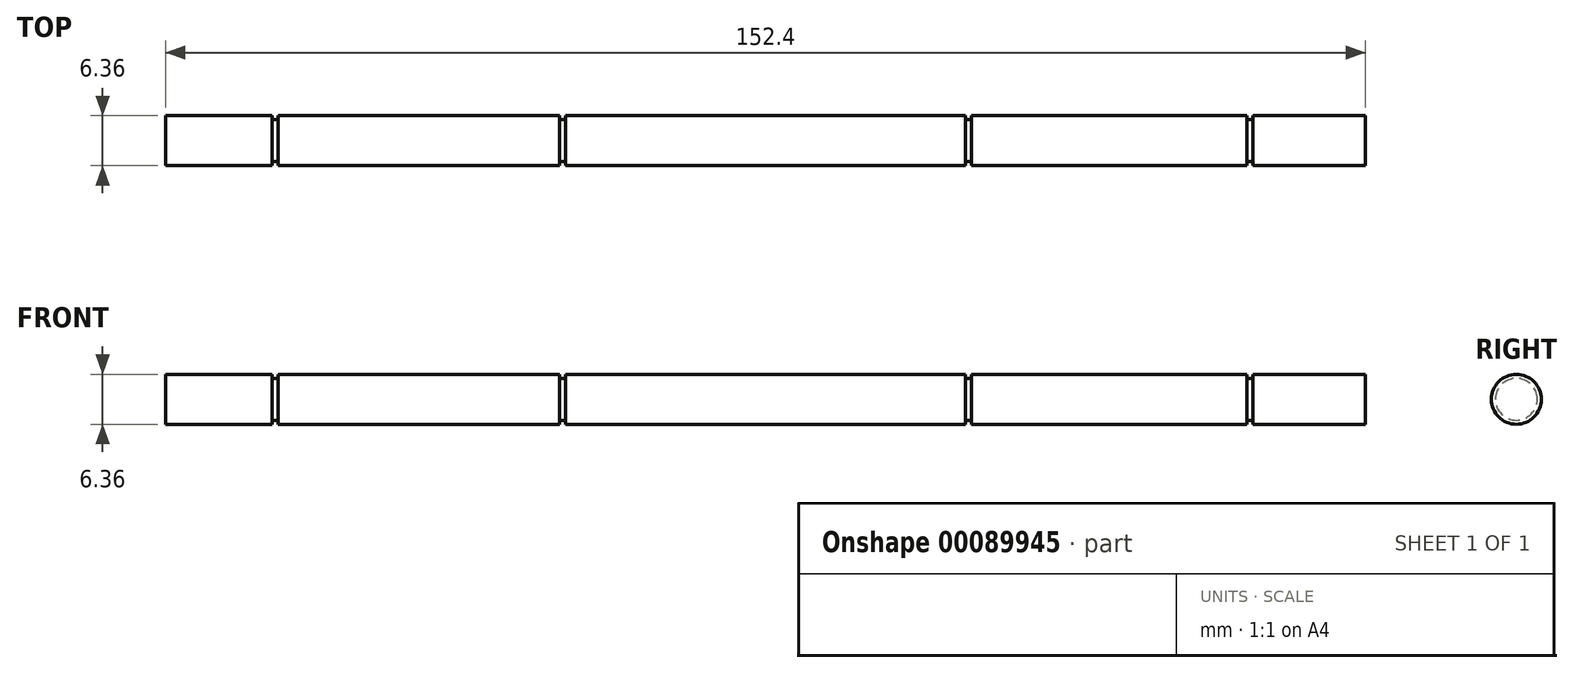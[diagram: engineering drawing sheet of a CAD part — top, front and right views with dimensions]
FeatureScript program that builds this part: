
annotation { "Feature Type Name" : "Feature", "Feature Type Description" : "" }
export const myFeature = defineFeature(function(context is Context, id is Id, definition is map)
    precondition{}
    {
        {
            var Q0;
            Q0=qCreatedBy(makeId("Right.planeOp"),FACE);
            var sketch = newSketch(context, id + "F0", { "sketchPlane" : qUnion([Q0])});
            skCircle(sketch, "E0", {"center": v(0, 0) * mm, "radius": 3.18 * mm});
            skSolve(sketch);
        }
        {
            var Q0;
            Q0 = qSketchRegion(id + "F0", true);
            extrude(context, id + "F1", {"entities" : qUnion([Q0]), "depth" : 152.4 * mm});
        }
        {
            var Q0;
            Q0=makeQuery(id+"F1.opExtrude","CAP_FACE",FACE,{"disambiguationData":[OSD([sQuery(id+"F0.wireOp",EDGE,"E0")])],"isStart":false});
            cPlane(context, id + "F2", {"entities" : qUnion([Q0]), "cplaneType" : CPlaneType.OFFSET, "offset" : 14.29 * mm, "oppositeDirection" : true, "width" : 152.4 * mm, "height" : 152.4 * mm});
        }
        {
            var Q0;
            Q0=qCreatedBy(id+"F2.planeOp",FACE);
            var sketch = newSketch(context, id + "F3", { "sketchPlane" : qUnion([Q0])});
            skCircle(sketch, "E1", {"center": v(0, 0) * mm, "radius": 3.18 * mm});
            skCircle(sketch, "E2", {"center": v(0, 0) * mm, "radius": 2.67 * mm});
            skSolve(sketch);
        }
        {
            var Q0;
            Q0 = qSketchRegion(id + "F3", true);
            extrude(context, id + "F4", {"entities" : qUnion([Q0]), "operationType" : NewBodyOperationType.REMOVE, "oppositeDirection" : true, "depth" : 0.74 * mm});
        }
        {
            var Q0;
            Q0=makeQuery(id+"F1.opExtrude","CAP_FACE",FACE,{"disambiguationData":[OSD([sQuery(id+"F0.wireOp",EDGE,"E0")])],"isStart":true});
            cPlane(context, id + "F5", {"entities" : qUnion([Q0]), "cplaneType" : CPlaneType.OFFSET, "offset" : 14.29 * mm, "oppositeDirection" : true, "width" : 152.4 * mm, "height" : 152.4 * mm});
        }
        {
            var Q0;
            Q0=qCreatedBy(id+"F5.planeOp",FACE);
            var sketch = newSketch(context, id + "F6", { "sketchPlane" : qUnion([Q0])});
            skCircle(sketch, "E3", {"center": v(0, 0) * mm, "radius": 3.18 * mm});
            skCircle(sketch, "E4", {"center": v(0, 0) * mm, "radius": 2.67 * mm});
            skSolve(sketch);
        }
        {
            var Q0;
            Q0 = qSketchRegion(id + "F6", true);
            extrude(context, id + "F7", {"entities" : qUnion([Q0]), "operationType" : NewBodyOperationType.REMOVE, "depth" : 0.74 * mm});
        }
        {
            var Q0;
            Q0=qCreatedBy(makeId("Right.planeOp"),FACE);
            cPlane(context, id + "F8", {"entities" : qUnion([Q0]), "cplaneType" : CPlaneType.OFFSET, "offset" : 50.8 * mm, "width" : 152.4 * mm, "height" : 152.4 * mm});
        }
        {
            var Q0;
            Q0=qCreatedBy(id+"F8.planeOp",FACE);
            var sketch = newSketch(context, id + "F9", { "sketchPlane" : qUnion([Q0])});
            skCircle(sketch, "E5", {"center": v(0, 0) * mm, "radius": 3.18 * mm});
            skCircle(sketch, "E6", {"center": v(0, 0) * mm, "radius": 2.67 * mm});
            skSolve(sketch);
        }
        {
            var Q0;
            Q0 = qSketchRegion(id + "F9", true);
            extrude(context, id + "F10", {"entities" : qUnion([Q0]), "operationType" : NewBodyOperationType.REMOVE, "oppositeDirection" : true, "depth" : 0.74 * mm});
        }
        {
            var Q0;
            Q0=makeQuery(id+"F1.opExtrude","CAP_FACE",FACE,{"disambiguationData":[OSD([sQuery(id+"F0.wireOp",EDGE,"E0")])],"isStart":false});
            cPlane(context, id + "F11", {"entities" : qUnion([Q0]), "cplaneType" : CPlaneType.OFFSET, "offset" : 50.8 * mm, "oppositeDirection" : true, "width" : 152.4 * mm, "height" : 152.4 * mm});
        }
        {
            var Q0;
            Q0=qCreatedBy(id+"F11.planeOp",FACE);
            var sketch = newSketch(context, id + "F12", { "sketchPlane" : qUnion([Q0])});
            skCircle(sketch, "E7", {"center": v(0, 0) * mm, "radius": 3.18 * mm});
            skCircle(sketch, "E8", {"center": v(0, 0) * mm, "radius": 2.67 * mm});
            skSolve(sketch);
        }
        {
            var Q0;
            Q0 = qSketchRegion(id + "F12", true);
            extrude(context, id + "F13", {"entities" : qUnion([Q0]), "operationType" : NewBodyOperationType.REMOVE, "depth" : 0.74 * mm});
        }
    });
